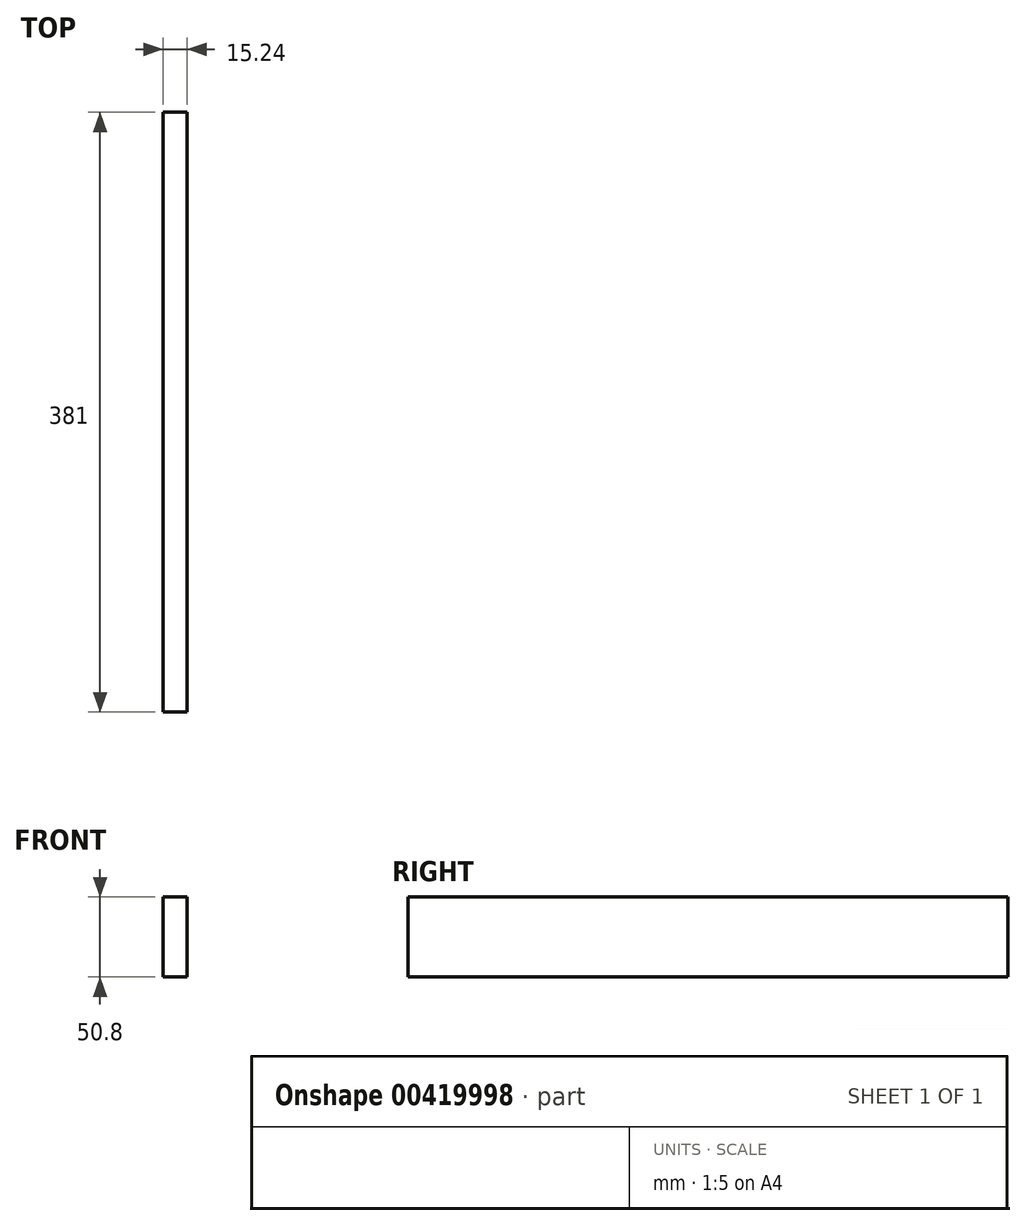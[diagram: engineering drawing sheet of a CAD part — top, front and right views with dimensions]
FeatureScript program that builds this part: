
annotation { "Feature Type Name" : "Feature", "Feature Type Description" : "" }
export const myFeature = defineFeature(function(context is Context, id is Id, definition is map)
    precondition{}
    {
        {
            var Q0;
            Q0=qCreatedBy(makeId("Front.planeOp"),FACE);
            var sketch = newSketch(context, id + "F0", { "sketchPlane" : qUnion([Q0])});
            skLineSegment(sketch, "E0.bottom", {"start": v(7.62, -25.4) * mm, "end": v(-7.62, -25.4) * mm});
            skLineSegment(sketch, "E0.top", {"start": v(7.62, 25.4) * mm, "end": v(-7.62, 25.4) * mm});
            skLineSegment(sketch, "E0.left", {"start": v(7.62, -25.4) * mm, "end": v(7.62, 25.4) * mm});
            skLineSegment(sketch, "E0.right", {"start": v(-7.62, -25.4) * mm, "end": v(-7.62, 25.4) * mm});
            skPoint(sketch, "E0.middle", {"position": v(0, 0) * mm});
            skSolve(sketch);
        }
        {
            var Q0;
            Q0=makeQuery(id+"F0.imprint","IMPRINT",FACE,{"disambiguationData":[TD([[makeQuery(id+"F0.imprint","IMPRINT",EDGE,{"derivedFrom":sQuery(id+"F0.wireOp",EDGE,"E0.bottom")}),-1.0]])]});
            extrude(context, id + "F1", {"entities" : qUnion([Q0]), "depth" : 381 * mm});
        }
    });
